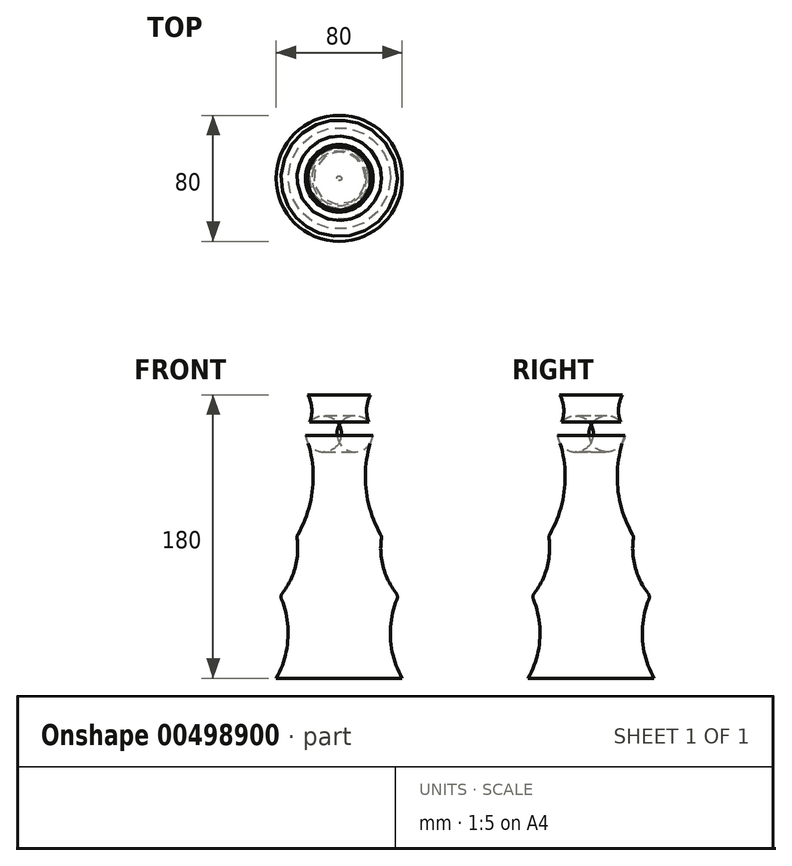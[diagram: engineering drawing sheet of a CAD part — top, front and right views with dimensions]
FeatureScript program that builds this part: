
annotation { "Feature Type Name" : "Feature", "Feature Type Description" : "" }
export const myFeature = defineFeature(function(context is Context, id is Id, definition is map)
    precondition{}
    {
        {
            var Q0;
            Q0=qCreatedBy(makeId("Front.planeOp"),FACE);
            var sketch = newSketch(context, id + "F0", { "sketchPlane" : qUnion([Q0])});
            skLineSegment(sketch, "E0", {"start": v(0, 0) * mm, "end": v(40, 0) * mm});
            skLineSegment(sketch, "E1", {"start": v(0, 0) * mm, "end": v(0, 180) * mm});
            skArc(sketch, "E2", {"start": v(37.58, 52.21) * mm, "mid": v(32.54, 25.82) * mm, "end": v(40, 0) * mm});
            skArc(sketch, "E3", {"start": v(27, 90.14) * mm, "mid": v(28.1, 70) * mm, "end": v(37.58, 52.21) * mm});
            skArc(sketch, "E4", {"start": v(21.42, 154.15) * mm, "mid": v(16.83, 121.5) * mm, "end": v(27, 90.14) * mm});
            skArc(sketch, "E5", {"start": v(21.42, 154.15) * mm, "mid": v(20.95, 158.63) * mm, "end": v(18.8, 162.58) * mm});
            skLineSegment(sketch, "E6", {"start": v(0, 180) * mm, "end": v(20, 180) * mm});
            skArc(sketch, "E7", {"start": v(20, 180) * mm, "mid": v(17.42, 171.43) * mm, "end": v(18.8, 162.58) * mm});
            skLineSegment(sketch, "E8", {"start": v(0, 107.4) * mm, "end": v(0, -8.91) * mm, "construction": true});
            skSolve(sketch);
        }
        {
            var Q0;
            Q0=makeQuery(id+"F0.imprint","IMPRINT",FACE,{"disambiguationData":[TD([[makeQuery(id+"F0.imprint","IMPRINT",EDGE,{"derivedFrom":sQuery(id+"F0.wireOp",EDGE,"E0")}),1.0]])]});
            var Q1;
            Q1=sQuery(id+"F0.wireOp",EDGE,"E8");
            revolve(context, id + "F1", {"entities" : qUnion([Q0]), "axis" : qUnion([Q1]), "revolveType" : RevolveType.FULL});
        }
        {
            var Q0;
            Q0=makeQuery(id+"F1.opRevolve","SWEPT_EDGE",EDGE,{"disambiguationData":[OSD([sQuery(id+"F0.wireOp",EDGE,"E2"),sQuery(id+"F0.wireOp",EDGE,"E3")])]});
            var Q1;
            Q1=makeQuery(id+"F1.opRevolve","SWEPT_EDGE",EDGE,{"disambiguationData":[OSD([sQuery(id+"F0.wireOp",EDGE,"E3"),sQuery(id+"F0.wireOp",EDGE,"E4")])]});
            fillet(context, id + "F2", {"entities" : qUnion([Q0, Q1]), "radius" : 4 * mm, "tangentPropagation" : true, "allowEdgeOverflow" : false});
        }
    });
